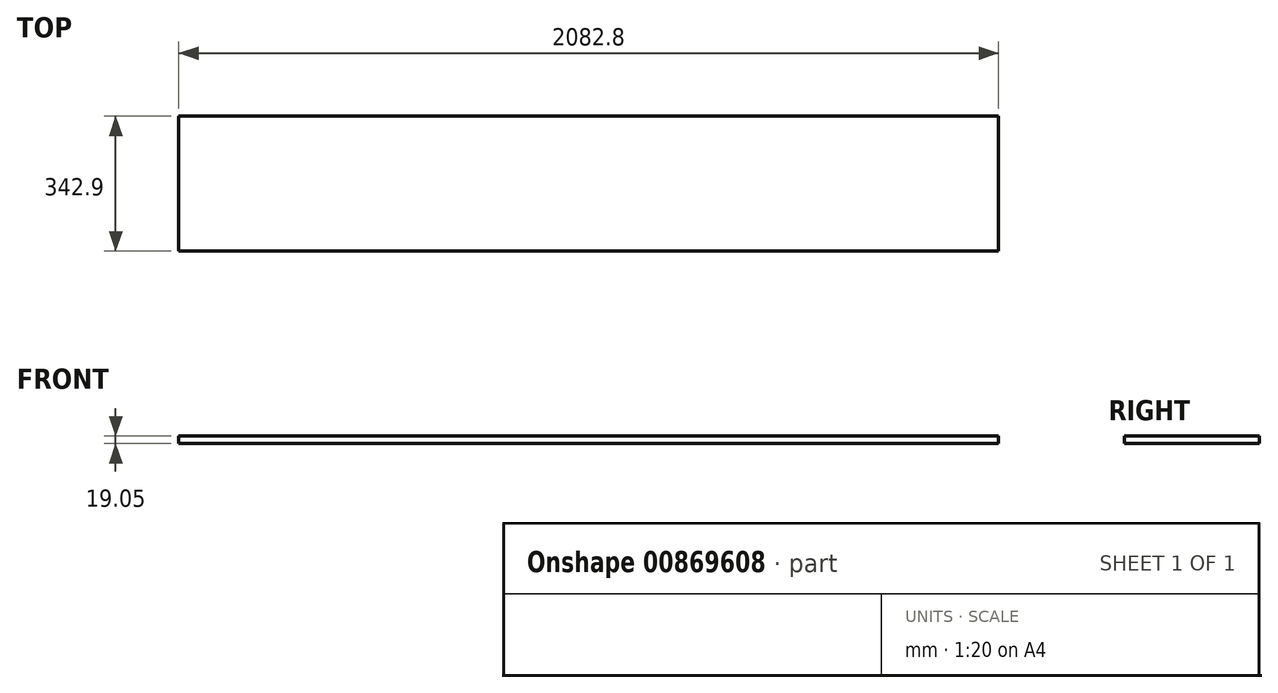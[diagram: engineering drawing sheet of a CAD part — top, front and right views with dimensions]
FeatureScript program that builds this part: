
annotation { "Feature Type Name" : "Feature", "Feature Type Description" : "" }
export const myFeature = defineFeature(function(context is Context, id is Id, definition is map)
    precondition{}
    {
        {
            var Q0;
            Q0=qCreatedBy(makeId("Top.planeOp"),FACE);
            var sketch = newSketch(context, id + "F0", { "sketchPlane" : qUnion([Q0])});
            skLineSegment(sketch, "E0.bottom", {"start": v(1.42, 0) * mm, "end": v(2084.22, 0) * mm});
            skLineSegment(sketch, "E0.top", {"start": v(1.42, -342.9) * mm, "end": v(2084.22, -342.9) * mm});
            skLineSegment(sketch, "E0.left", {"start": v(1.42, 0) * mm, "end": v(1.42, -342.9) * mm});
            skLineSegment(sketch, "E0.right", {"start": v(2084.22, 0) * mm, "end": v(2084.22, -342.9) * mm});
            skSolve(sketch);
        }
        {
            var Q0;
            Q0 = qSketchRegion(id + "F0", true);
            extrude(context, id + "F1", {"entities" : qUnion([Q0]), "depth" : 19.05 * mm, "offsetDistance" : 25.4 * mm});
        }
    });
